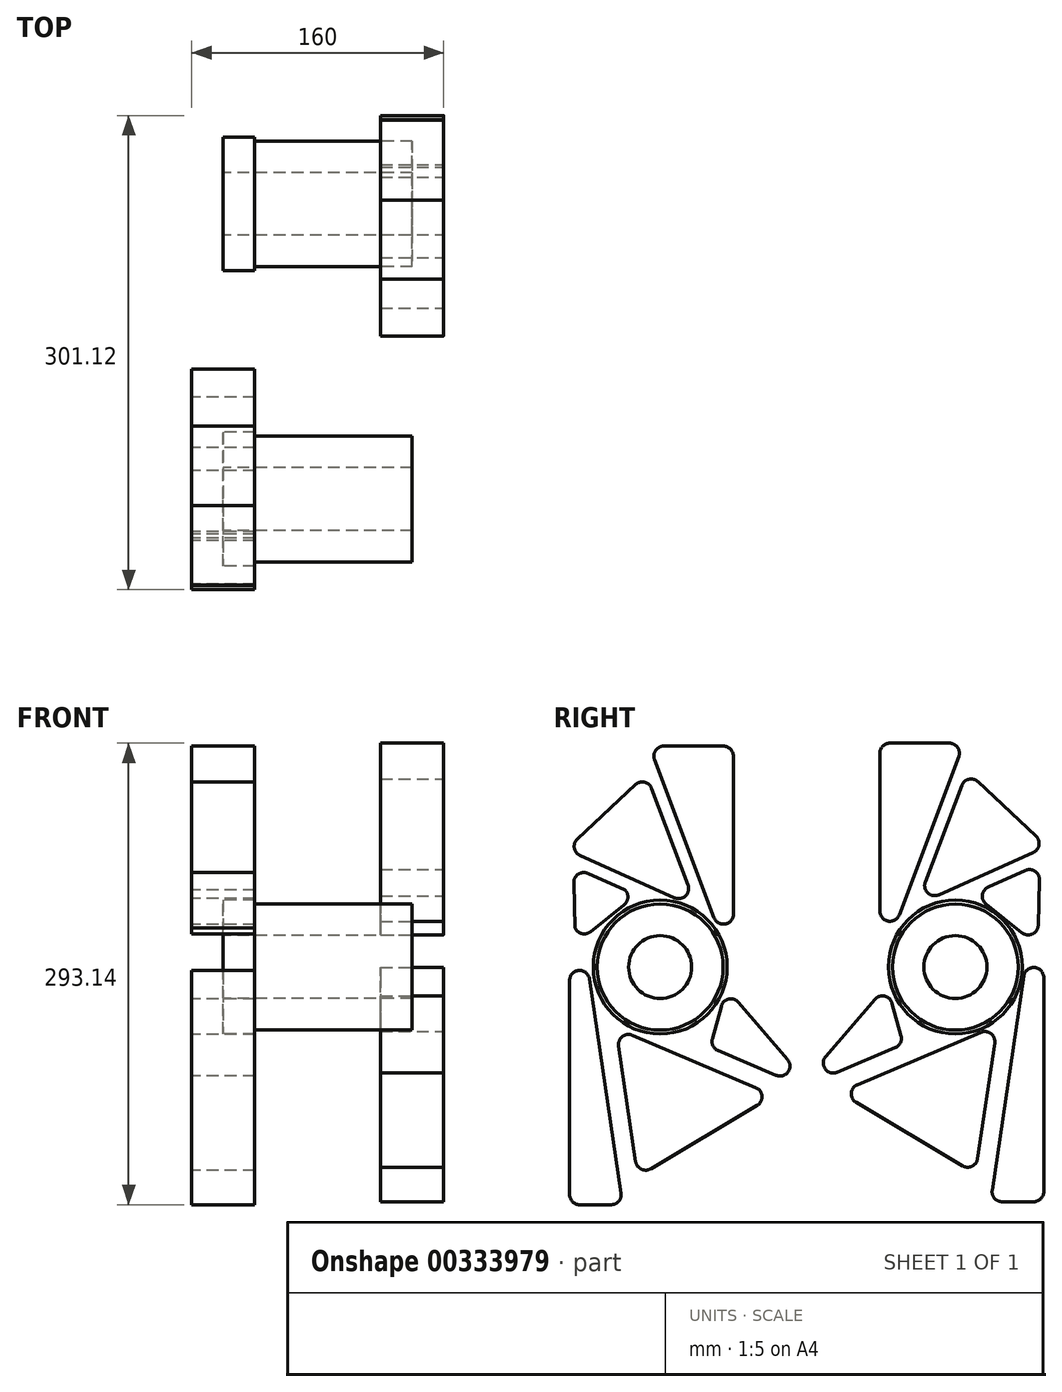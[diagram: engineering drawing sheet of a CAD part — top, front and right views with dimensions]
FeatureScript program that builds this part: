
annotation { "Feature Type Name" : "Feature", "Feature Type Description" : "" }
export const myFeature = defineFeature(function(context is Context, id is Id, definition is map)
    precondition{}
    {
        {
            var Q0;
            Q0=qCreatedBy(makeId("Right.planeOp"),FACE);
            var sketch = newSketch(context, id + "F0", { "sketchPlane" : qUnion([Q0])});
            skLineSegment(sketch, "E0", {"start": v(-158.75, 0) * mm, "end": v(-158.75, 250) * mm});
            skLineSegment(sketch, "E1", {"start": v(-158.75, 250) * mm, "end": v(-93.75, 312.25) * mm});
            skLineSegment(sketch, "E2.MirrorCS", {"start": v(158.75, 250) * mm, "end": v(93.75, 312.25) * mm});
            skLineSegment(sketch, "E3.MirrorCS", {"start": v(158.75, 0) * mm, "end": v(158.75, 250) * mm});
            skLineSegment(sketch, "E4", {"start": v(-158.75, 0) * mm, "end": v(-107.95, 0) * mm});
            skArc(sketch, "E5", {"start": v(107.95, 0) * mm, "mid": v(0, 60.1) * mm, "end": v(-107.95, 0) * mm});
            skLineSegment(sketch, "E6", {"start": v(107.95, 0) * mm, "end": v(158.75, 0) * mm});
            skLineSegment(sketch, "E7", {"start": v(-93.75, 312.25) * mm, "end": v(-40, 312.25) * mm});
            skLineSegment(sketch, "E8", {"start": v(-40, 312.25) * mm, "end": v(-40, 159.85) * mm});
            skArc(sketch, "E9", {"start": v(-40, 159.85) * mm, "mid": v(0, 119.85) * mm, "end": v(40, 159.85) * mm});
            skLineSegment(sketch, "E10", {"start": v(40, 159.85) * mm, "end": v(40, 312.25) * mm});
            skLineSegment(sketch, "E11", {"start": v(40, 312.25) * mm, "end": v(93.75, 312.25) * mm});
            skCircle(sketch, "E12", {"center": v(93.75, 159.85) * mm, "radius": 40 * mm});
            skCircle(sketch, "E13", {"center": v(-93.75, 159.85) * mm, "radius": 40 * mm});
            skSolve(sketch);
        }
        {
            var Q0;
            Q0=makeQuery(id+"F0.imprint","IMPRINT",FACE,{"disambiguationData":[TD([[makeQuery(id+"F0.imprint","IMPRINT",EDGE,{"derivedFrom":sQuery(id+"F0.wireOp",EDGE,"E0")}),-1.0]])]});
            extrude(context, id + "F1", {"entities" : qUnion([Q0]), "endBound" : BoundingType.SYMMETRIC, "depth" : 160 * mm});
        }
        {
            var Q0;
            Q0=makeQuery(id+"F1.opExtrude","SWEPT_FACE",FACE,{"disambiguationData":[OSD([sQuery(id+"F0.wireOp",EDGE,"E3.MirrorCS")])]});
            var sketch = newSketch(context, id + "F2", { "sketchPlane" : qUnion([Q0])});
            skLineSegment(sketch, "E14.bottom", {"start": v(-40, 0) * mm, "end": v(40, 0) * mm});
            skLineSegment(sketch, "E14.top", {"start": v(-40, 330.24) * mm, "end": v(40, 330.24) * mm});
            skLineSegment(sketch, "E14.left", {"start": v(-40, 0) * mm, "end": v(-40, 330.24) * mm});
            skLineSegment(sketch, "E14.right", {"start": v(40, 0) * mm, "end": v(40, 330.24) * mm});
            skSolve(sketch);
        }
        {
            var Q0;
            {var subQ0=sQuery(id+"F2.wireOp",EDGE,"E14.bottom");Q0=makeQuery(id+"F2.imprint","IMPRINT",FACE,{"disambiguationData":[TD([[makeQuery(id+"F2.imprint","IMPRINT",EDGE,{"derivedFrom":subQ0}),1.0]])]});}
            var Q1;
            {var subQ0=sQuery(id+"F2.wireOp",EDGE,"E14.top");Q1=makeQuery(id+"F2.imprint","IMPRINT",FACE,{"disambiguationData":[TD([[makeQuery(id+"F2.imprint","IMPRINT",EDGE,{"derivedFrom":subQ0}),-1.0]])]});}
            extrude(context, id + "F3", {"entities" : qUnion([Q0, Q1]), "operationType" : NewBodyOperationType.REMOVE, "oppositeDirection" : true, "depth" : 414.02 * mm});
        }
        {
            var Q0;
            Q0=makeQuery(id+"F1.opExtrude","CAP_FACE",FACE,{"disambiguationData":[OSD([sQuery(id+"F0.wireOp",EDGE,"E0"),sQuery(id+"F0.wireOp",EDGE,"E1"),sQuery(id+"F0.wireOp",EDGE,"E2.MirrorCS"),sQuery(id+"F0.wireOp",EDGE,"E3.MirrorCS"),sQuery(id+"F0.wireOp",EDGE,"E4"),sQuery(id+"F0.wireOp",EDGE,"E5"),sQuery(id+"F0.wireOp",EDGE,"E6"),sQuery(id+"F0.wireOp",EDGE,"E7"),sQuery(id+"F0.wireOp",EDGE,"E8"),sQuery(id+"F0.wireOp",EDGE,"E9"),sQuery(id+"F0.wireOp",EDGE,"E10"),sQuery(id+"F0.wireOp",EDGE,"E11"),sQuery(id+"F0.wireOp",EDGE,"E12"),sQuery(id+"F0.wireOp",EDGE,"E13")])],"isStart":true});
            var sketch = newSketch(context, id + "F4", { "sketchPlane" : qUnion([Q0])});
            skCircle(sketch, "E15", {"center": v(-93.75, 159.85) * mm, "radius": 42.5 * mm});
            skCircle(sketch, "E16", {"center": v(-93.75, 159.85) * mm, "radius": 20 * mm});
            skCircle(sketch, "E17", {"center": v(93.75, 159.85) * mm, "radius": 42.5 * mm});
            skCircle(sketch, "E18", {"center": v(93.75, 159.85) * mm, "radius": 20 * mm});
            skSolve(sketch);
        }
        {
            var Q0;
            Q0=makeQuery(id+"F4.imprint","IMPRINT",FACE,{"disambiguationData":[TD([[makeQuery(id+"F4.imprint","IMPRINT",EDGE,{"derivedFrom":sQuery(id+"F4.wireOp",EDGE,"E16")}),-1.0]])]});
            var Q1;
            Q1=makeQuery(id+"F4.imprint","IMPRINT",FACE,{"disambiguationData":[TD([[makeQuery(id+"F4.imprint","IMPRINT",EDGE,{"derivedFrom":sQuery(id+"F4.wireOp",EDGE,"E18")}),-1.0]])]});
            extrude(context, id + "F5", {"entities" : qUnion([Q0, Q1]), "operationType" : NewBodyOperationType.ADD, "oppositeDirection" : true, "depth" : 140 * mm});
        }
        {
            var Q0;
            {var subQ0=sQuery(id+"F0.wireOp",EDGE,"E13");var subQ1=sQuery(id+"F0.wireOp",EDGE,"E12");Q0=makeQuery(id+"F5.boolean.opBoolean","MERGE",FACE,{"derivedFrom":[makeQuery(id+"F1.opExtrude","CAP_FACE",FACE,{"disambiguationData":[OSD([sQuery(id+"F0.wireOp",EDGE,"E0"),sQuery(id+"F0.wireOp",EDGE,"E1"),sQuery(id+"F0.wireOp",EDGE,"E2.MirrorCS"),sQuery(id+"F0.wireOp",EDGE,"E3.MirrorCS"),sQuery(id+"F0.wireOp",EDGE,"E4"),sQuery(id+"F0.wireOp",EDGE,"E5"),sQuery(id+"F0.wireOp",EDGE,"E6"),sQuery(id+"F0.wireOp",EDGE,"E7"),sQuery(id+"F0.wireOp",EDGE,"E8"),sQuery(id+"F0.wireOp",EDGE,"E9"),sQuery(id+"F0.wireOp",EDGE,"E10"),sQuery(id+"F0.wireOp",EDGE,"E11"),subQ1,subQ0])],"isStart":true}),makeQuery(id+"F5.opExtrude","CAP_FACE",FACE,{"disambiguationData":[OSD([subQ1,sQuery(id+"F4.wireOp",EDGE,"E16")])],"isStart":true}),makeQuery(id+"F5.opExtrude","CAP_FACE",FACE,{"disambiguationData":[OSD([subQ0,sQuery(id+"F4.wireOp",EDGE,"E18")])],"isStart":true})]});}
            var sketch = newSketch(context, id + "F6", { "sketchPlane" : qUnion([Q0])});
            skCircle(sketch, "E19", {"center": v(-93.75, 159.85) * mm, "radius": 42.5 * mm});
            skCircle(sketch, "E20", {"center": v(93.75, 159.85) * mm, "radius": 42.5 * mm});
            skSolve(sketch);
        }
        {
            var Q0;
            Q0=makeQuery(id+"F6.imprint","IMPRINT",FACE,{"disambiguationData":[TD([[makeQuery(id+"F6.imprint","IMPRINT",EDGE,{"derivedFrom":sQuery(id+"F6.wireOp",EDGE,"E19")}),1.0]])]});
            var Q1;
            Q1=makeQuery(id+"F6.imprint","IMPRINT",FACE,{"disambiguationData":[TD([[makeQuery(id+"F6.imprint","IMPRINT",EDGE,{"derivedFrom":sQuery(id+"F6.wireOp",EDGE,"E20")}),1.0]])]});
            extrude(context, id + "F7", {"entities" : qUnion([Q0, Q1]), "operationType" : NewBodyOperationType.REMOVE, "oppositeDirection" : true, "depth" : 20 * mm});
        }
        {
            var Q0;
            Q0=makeQuery(id+"F1.opExtrude","CAP_FACE",FACE,{"disambiguationData":[OSD([sQuery(id+"F0.wireOp",EDGE,"E0"),sQuery(id+"F0.wireOp",EDGE,"E1"),sQuery(id+"F0.wireOp",EDGE,"E2.MirrorCS"),sQuery(id+"F0.wireOp",EDGE,"E3.MirrorCS"),sQuery(id+"F0.wireOp",EDGE,"E4"),sQuery(id+"F0.wireOp",EDGE,"E5"),sQuery(id+"F0.wireOp",EDGE,"E6"),sQuery(id+"F0.wireOp",EDGE,"E7"),sQuery(id+"F0.wireOp",EDGE,"E8"),sQuery(id+"F0.wireOp",EDGE,"E9"),sQuery(id+"F0.wireOp",EDGE,"E10"),sQuery(id+"F0.wireOp",EDGE,"E11"),sQuery(id+"F0.wireOp",EDGE,"E12"),sQuery(id+"F0.wireOp",EDGE,"E13")])],"isStart":false});
            var sketch = newSketch(context, id + "F8", { "sketchPlane" : qUnion([Q0])});
            skLineSegment(sketch, "E21", {"start": v(-89.93, 302.05) * mm, "end": v(-52.17, 302.05) * mm});
            skLineSegment(sketch, "E22", {"start": v(-45.82, 295.7) * mm, "end": v(-45.82, 195.28) * mm});
            skLineSegment(sketch, "E23", {"start": v(-58.11, 193.04) * mm, "end": v(-95.87, 293.47) * mm});
            skPoint(sketch, "E24.visualSharp", {"position": v(-99.1, 302.05) * mm});
            skArc(sketch, "E24.filletArc", {"start": v(-89.93, 302.05) * mm, "mid": v(-95.15, 299.32) * mm, "end": v(-95.87, 293.47) * mm});
            skPoint(sketch, "E25.visualSharp", {"position": v(-45.82, 302.05) * mm});
            skArc(sketch, "E25.filletArc", {"start": v(-45.82, 295.7) * mm, "mid": v(-47.68, 300.2) * mm, "end": v(-52.17, 302.05) * mm});
            skPoint(sketch, "E26.visualSharp", {"position": v(-45.82, 160.34) * mm});
            skArc(sketch, "E26.filletArc", {"start": v(-58.11, 193.04) * mm, "mid": v(-51.03, 189.03) * mm, "end": v(-45.82, 195.28) * mm});
            skLineSegment(sketch, "E27", {"start": v(-108.02, 277.59) * mm, "end": v(-144.9, 243.03) * mm});
            skLineSegment(sketch, "E28", {"start": v(-143.16, 232.6) * mm, "end": v(-83.18, 205.71) * mm});
            skLineSegment(sketch, "E29", {"start": v(-74.64, 213.74) * mm, "end": v(-97.74, 275.19) * mm});
            skPoint(sketch, "E30.visualSharp", {"position": v(-101.08, 284.09) * mm});
            skArc(sketch, "E30.filletArc", {"start": v(-97.74, 275.19) * mm, "mid": v(-102.24, 279.14) * mm, "end": v(-108.02, 277.59) * mm});
            skPoint(sketch, "E31.visualSharp", {"position": v(-151.87, 236.5) * mm});
            skArc(sketch, "E31.filletArc", {"start": v(-144.9, 243.03) * mm, "mid": v(-146.83, 237.35) * mm, "end": v(-143.16, 232.6) * mm});
            skPoint(sketch, "E32.visualSharp", {"position": v(-69.27, 199.48) * mm});
            skArc(sketch, "E32.filletArc", {"start": v(-83.18, 205.71) * mm, "mid": v(-76.23, 206.88) * mm, "end": v(-74.64, 213.74) * mm});
            skLineSegment(sketch, "E33", {"start": v(-138.24, 221.2) * mm, "end": v(-114.6, 210.6) * mm});
            skLineSegment(sketch, "E34", {"start": v(-113.24, 199.85) * mm, "end": v(-136.05, 181.64) * mm});
            skLineSegment(sketch, "E35", {"start": v(-146.36, 186.43) * mm, "end": v(-147.18, 215.23) * mm});
            skPoint(sketch, "E36.visualSharp", {"position": v(-147.47, 225.34) * mm});
            skArc(sketch, "E36.filletArc", {"start": v(-138.24, 221.2) * mm, "mid": v(-144.36, 220.7) * mm, "end": v(-147.18, 215.23) * mm});
            skPoint(sketch, "E37.visualSharp", {"position": v(-146, 173.7) * mm});
            skArc(sketch, "E37.filletArc", {"start": v(-146.36, 186.43) * mm, "mid": v(-142.68, 180.85) * mm, "end": v(-136.05, 181.64) * mm});
            skPoint(sketch, "E38.visualSharp", {"position": v(-105.1, 206.35) * mm});
            skArc(sketch, "E38.filletArc", {"start": v(-113.24, 199.85) * mm, "mid": v(-110.9, 205.61) * mm, "end": v(-114.6, 210.6) * mm});
            skLineSegment(sketch, "E39", {"start": v(-143.5, 10.77) * mm, "end": v(-123.4, 10.77) * mm});
            skLineSegment(sketch, "E40", {"start": v(-117.1, 18.05) * mm, "end": v(-137.21, 154.14) * mm});
            skLineSegment(sketch, "E41", {"start": v(-149.84, 153.21) * mm, "end": v(-149.84, 17.12) * mm});
            skPoint(sketch, "E42.visualSharp", {"position": v(-149.84, 239.66) * mm});
            skArc(sketch, "E42.filletArc", {"start": v(-137.21, 154.14) * mm, "mid": v(-143.96, 159.54) * mm, "end": v(-149.84, 153.21) * mm});
            skPoint(sketch, "E43.visualSharp", {"position": v(-149.84, 10.77) * mm});
            skArc(sketch, "E43.filletArc", {"start": v(-149.84, 17.12) * mm, "mid": v(-147.98, 12.63) * mm, "end": v(-143.5, 10.77) * mm});
            skPoint(sketch, "E44.visualSharp", {"position": v(-116.03, 10.77) * mm});
            skArc(sketch, "E44.filletArc", {"start": v(-123.4, 10.77) * mm, "mid": v(-118.58, 12.97) * mm, "end": v(-117.1, 18.05) * mm});
            skLineSegment(sketch, "E45", {"start": v(-109.94, 118.4) * mm, "end": v(-31.51, 85.1) * mm});
            skLineSegment(sketch, "E46", {"start": v(-30.74, 73.8) * mm, "end": v(-98.32, 33.57) * mm});
            skLineSegment(sketch, "E47", {"start": v(-107.85, 38.1) * mm, "end": v(-118.7, 111.62) * mm});
            skPoint(sketch, "E48.visualSharp", {"position": v(-120.36, 122.82) * mm});
            skArc(sketch, "E48.filletArc", {"start": v(-109.94, 118.4) * mm, "mid": v(-116.3, 117.57) * mm, "end": v(-118.7, 111.62) * mm});
            skPoint(sketch, "E49.visualSharp", {"position": v(-19.98, 80.2) * mm});
            skArc(sketch, "E49.filletArc", {"start": v(-30.74, 73.8) * mm, "mid": v(-27.66, 79.68) * mm, "end": v(-31.51, 85.1) * mm});
            skPoint(sketch, "E50.visualSharp", {"position": v(-106.46, 28.72) * mm});
            skArc(sketch, "E50.filletArc", {"start": v(-107.85, 38.1) * mm, "mid": v(-104.29, 33.29) * mm, "end": v(-98.32, 33.57) * mm});
            skLineSegment(sketch, "E51", {"start": v(-55.6, 108.64) * mm, "end": v(-18.68, 92.97) * mm});
            skLineSegment(sketch, "E52", {"start": v(-11.38, 102.95) * mm, "end": v(-42.61, 139.31) * mm});
            skLineSegment(sketch, "E53", {"start": v(-53.55, 136.86) * mm, "end": v(-59.24, 116.17) * mm});
            skPoint(sketch, "E54.visualSharp", {"position": v(-50.39, 148.37) * mm});
            skArc(sketch, "E54.filletArc", {"start": v(-42.61, 139.31) * mm, "mid": v(-48.82, 141.37) * mm, "end": v(-53.55, 136.86) * mm});
            skPoint(sketch, "E55.visualSharp", {"position": v(-60.7, 110.81) * mm});
            skArc(sketch, "E55.filletArc", {"start": v(-59.24, 116.17) * mm, "mid": v(-58.83, 111.72) * mm, "end": v(-55.6, 108.64) * mm});
            skPoint(sketch, "E56.visualSharp", {"position": v(6.3, 82.37) * mm});
            skArc(sketch, "E56.filletArc", {"start": v(-18.68, 92.97) * mm, "mid": v(-11.07, 95.07) * mm, "end": v(-11.38, 102.95) * mm});
            skArc(sketch, "E57.MirrorCS", {"start": v(138.24, 221.2) * mm, "mid": v(144.36, 220.7) * mm, "end": v(147.18, 215.23) * mm});
            skArc(sketch, "E58.MirrorCS", {"start": v(45.82, 295.7) * mm, "mid": v(47.68, 300.2) * mm, "end": v(52.17, 302.05) * mm});
            skArc(sketch, "E59.MirrorCS", {"start": v(59.24, 116.17) * mm, "mid": v(58.83, 111.72) * mm, "end": v(55.6, 108.64) * mm});
            skArc(sketch, "E60.MirrorCS", {"start": v(97.74, 275.19) * mm, "mid": v(102.24, 279.14) * mm, "end": v(108.02, 277.59) * mm});
            skArc(sketch, "E61.MirrorCS", {"start": v(144.9, 243.03) * mm, "mid": v(146.83, 237.35) * mm, "end": v(143.16, 232.6) * mm});
            skLineSegment(sketch, "E62.MirrorCS", {"start": v(146.36, 186.43) * mm, "end": v(147.18, 215.23) * mm});
            skArc(sketch, "E63.MirrorCS", {"start": v(89.93, 302.05) * mm, "mid": v(95.15, 299.32) * mm, "end": v(95.87, 293.47) * mm});
            skArc(sketch, "E64.MirrorCS", {"start": v(58.11, 193.04) * mm, "mid": v(51.03, 189.03) * mm, "end": v(45.82, 195.28) * mm});
            skLineSegment(sketch, "E65.MirrorCS", {"start": v(138.24, 221.2) * mm, "end": v(114.6, 210.6) * mm});
            skArc(sketch, "E66.MirrorCS", {"start": v(137.21, 154.14) * mm, "mid": v(143.96, 159.54) * mm, "end": v(149.84, 153.21) * mm});
            skLineSegment(sketch, "E67.MirrorCS", {"start": v(143.5, 10.77) * mm, "end": v(123.4, 10.77) * mm});
            skArc(sketch, "E68.MirrorCS", {"start": v(149.84, 17.12) * mm, "mid": v(147.98, 12.63) * mm, "end": v(143.5, 10.77) * mm});
            skLineSegment(sketch, "E69.MirrorCS", {"start": v(113.24, 199.85) * mm, "end": v(136.05, 181.64) * mm});
            skLineSegment(sketch, "E70.MirrorCS", {"start": v(143.16, 232.6) * mm, "end": v(83.18, 205.71) * mm});
            skArc(sketch, "E71.MirrorCS", {"start": v(83.18, 205.71) * mm, "mid": v(76.23, 206.88) * mm, "end": v(74.64, 213.74) * mm});
            skLineSegment(sketch, "E72.MirrorCS", {"start": v(53.55, 136.86) * mm, "end": v(59.24, 116.17) * mm});
            skArc(sketch, "E73.MirrorCS", {"start": v(146.36, 186.43) * mm, "mid": v(142.68, 180.85) * mm, "end": v(136.05, 181.64) * mm});
            skArc(sketch, "E74.MirrorCS", {"start": v(109.94, 118.4) * mm, "mid": v(116.3, 117.57) * mm, "end": v(118.7, 111.62) * mm});
            skArc(sketch, "E75.MirrorCS", {"start": v(107.85, 38.1) * mm, "mid": v(104.29, 33.29) * mm, "end": v(98.32, 33.57) * mm});
            skArc(sketch, "E76.MirrorCS", {"start": v(123.4, 10.77) * mm, "mid": v(118.58, 12.97) * mm, "end": v(117.1, 18.05) * mm});
            skArc(sketch, "E77.MirrorCS", {"start": v(42.61, 139.31) * mm, "mid": v(48.82, 141.37) * mm, "end": v(53.55, 136.86) * mm});
            skArc(sketch, "E78.MirrorCS", {"start": v(113.24, 199.85) * mm, "mid": v(110.9, 205.61) * mm, "end": v(114.6, 210.6) * mm});
            skArc(sketch, "E79.MirrorCS", {"start": v(30.74, 73.8) * mm, "mid": v(27.66, 79.68) * mm, "end": v(31.51, 85.1) * mm});
            skArc(sketch, "E80.MirrorCS", {"start": v(18.68, 92.97) * mm, "mid": v(11.07, 95.07) * mm, "end": v(11.38, 102.95) * mm});
            skLineSegment(sketch, "E81.MirrorCS", {"start": v(55.6, 108.64) * mm, "end": v(18.68, 92.97) * mm});
            skLineSegment(sketch, "E82.MirrorCS", {"start": v(89.93, 302.05) * mm, "end": v(52.17, 302.05) * mm});
            skPoint(sketch, "E83.MirrorP", {"position": v(69.27, 199.48) * mm});
            skLineSegment(sketch, "E84.MirrorCS", {"start": v(108.02, 277.59) * mm, "end": v(144.9, 243.03) * mm});
            skPoint(sketch, "E85.MirrorP", {"position": v(45.82, 302.05) * mm});
            skPoint(sketch, "E86.MirrorP", {"position": v(147.47, 225.34) * mm});
            skPoint(sketch, "E87.MirrorP", {"position": v(151.87, 236.5) * mm});
            skPoint(sketch, "E88.MirrorP", {"position": v(120.36, 122.82) * mm});
            skPoint(sketch, "E89.MirrorP", {"position": v(101.08, 284.09) * mm});
            skLineSegment(sketch, "E90.MirrorCS", {"start": v(109.94, 118.4) * mm, "end": v(31.51, 85.1) * mm});
            skLineSegment(sketch, "E91.MirrorCS", {"start": v(45.82, 295.7) * mm, "end": v(45.82, 195.28) * mm});
            skLineSegment(sketch, "E92.MirrorCS", {"start": v(58.11, 193.04) * mm, "end": v(95.87, 293.47) * mm});
            skLineSegment(sketch, "E93.MirrorCS", {"start": v(30.74, 73.8) * mm, "end": v(98.32, 33.57) * mm});
            skLineSegment(sketch, "E94.MirrorCS", {"start": v(117.1, 18.05) * mm, "end": v(137.21, 154.14) * mm});
            skPoint(sketch, "E95.MirrorP", {"position": v(19.98, 80.2) * mm});
            skLineSegment(sketch, "E96.MirrorCS", {"start": v(11.38, 102.95) * mm, "end": v(42.61, 139.31) * mm});
            skLineSegment(sketch, "E97.MirrorCS", {"start": v(74.64, 213.74) * mm, "end": v(97.74, 275.19) * mm});
            skPoint(sketch, "E98.MirrorP", {"position": v(-6.3, 82.37) * mm});
            skPoint(sketch, "E99.MirrorP", {"position": v(149.84, 239.66) * mm});
            skLineSegment(sketch, "E100.MirrorCS", {"start": v(107.85, 38.1) * mm, "end": v(118.7, 111.62) * mm});
            skPoint(sketch, "E101.MirrorP", {"position": v(106.46, 28.72) * mm});
            skLineSegment(sketch, "E102.MirrorCS", {"start": v(149.84, 153.21) * mm, "end": v(149.84, 17.12) * mm});
            skPoint(sketch, "E103.MirrorP", {"position": v(116.03, 10.77) * mm});
            skPoint(sketch, "E104.MirrorP", {"position": v(60.7, 110.81) * mm});
            skPoint(sketch, "E105.MirrorP", {"position": v(105.1, 206.35) * mm});
            skPoint(sketch, "E106.MirrorP", {"position": v(99.1, 302.05) * mm});
            skPoint(sketch, "E107.MirrorP", {"position": v(149.84, 10.77) * mm});
            skPoint(sketch, "E108.MirrorP", {"position": v(45.82, 160.34) * mm});
            skPoint(sketch, "E109.MirrorP", {"position": v(146, 173.7) * mm});
            skPoint(sketch, "E110.MirrorP", {"position": v(50.39, 148.37) * mm});
            skLineSegment(sketch, "E111", {"start": v(-6.25, 67.16) * mm, "end": v(6.25, 67.16) * mm});
            skLineSegment(sketch, "E112", {"start": v(11.4, 77.23) * mm, "end": v(5.14, 85.86) * mm});
            skLineSegment(sketch, "E113", {"start": v(-5.14, 85.86) * mm, "end": v(-11.4, 77.23) * mm});
            skPoint(sketch, "E114.visualSharp", {"position": v(0, 92.97) * mm});
            skArc(sketch, "E114.filletArc", {"start": v(5.14, 85.86) * mm, "mid": v(0, 88.49) * mm, "end": v(-5.14, 85.86) * mm});
            skPoint(sketch, "E115.visualSharp", {"position": v(18.68, 67.16) * mm});
            skArc(sketch, "E115.filletArc", {"start": v(6.25, 67.16) * mm, "mid": v(11.9, 70.62) * mm, "end": v(11.4, 77.23) * mm});
            skPoint(sketch, "E116.visualSharp", {"position": v(-18.68, 67.16) * mm});
            skArc(sketch, "E116.filletArc", {"start": v(-11.4, 77.23) * mm, "mid": v(-11.9, 70.62) * mm, "end": v(-6.25, 67.16) * mm});
            skSolve(sketch);
        }
        {
            var Q0;
            Q0=makeQuery(id+"F8.imprint","IMPRINT",FACE,{"disambiguationData":[TD([[makeQuery(id+"F8.imprint","IMPRINT",EDGE,{"derivedFrom":sQuery(id+"F8.wireOp",EDGE,"E27")}),1.0]])]});
            var Q1;
            Q1=makeQuery(id+"F8.imprint","IMPRINT",FACE,{"disambiguationData":[TD([[makeQuery(id+"F8.imprint","IMPRINT",EDGE,{"derivedFrom":sQuery(id+"F8.wireOp",EDGE,"E21")}),-1.0]])]});
            var Q2;
            Q2=makeQuery(id+"F8.imprint","IMPRINT",FACE,{"disambiguationData":[TD([[makeQuery(id+"F8.imprint","IMPRINT",EDGE,{"derivedFrom":sQuery(id+"F8.wireOp",EDGE,"E33")}),-1.0]])]});
            var Q3;
            Q3=makeQuery(id+"F8.imprint","IMPRINT",FACE,{"disambiguationData":[TD([[makeQuery(id+"F8.imprint","IMPRINT",EDGE,{"derivedFrom":sQuery(id+"F8.wireOp",EDGE,"E39")}),1.0]])]});
            var Q4;
            Q4=makeQuery(id+"F8.imprint","IMPRINT",FACE,{"disambiguationData":[TD([[makeQuery(id+"F8.imprint","IMPRINT",EDGE,{"derivedFrom":sQuery(id+"F8.wireOp",EDGE,"E45")}),-1.0]])]});
            var Q5;
            Q5=makeQuery(id+"F8.imprint","IMPRINT",FACE,{"disambiguationData":[TD([[makeQuery(id+"F8.imprint","IMPRINT",EDGE,{"derivedFrom":sQuery(id+"F8.wireOp",EDGE,"E51")}),1.0]])]});
            var Q6;
            Q6=makeQuery(id+"F8.imprint","IMPRINT",FACE,{"disambiguationData":[TD([[makeQuery(id+"F8.imprint","IMPRINT",EDGE,{"derivedFrom":sQuery(id+"F8.wireOp",EDGE,"E111")}),1.0]])]});
            var Q7;
            Q7=makeQuery(id+"F8.imprint","IMPRINT",FACE,{"disambiguationData":[TD([[makeQuery(id+"F8.imprint","IMPRINT",EDGE,{"derivedFrom":sQuery(id+"F8.wireOp",EDGE,"E59.MirrorCS")}),-1.0]])]});
            var Q8;
            Q8=makeQuery(id+"F8.imprint","IMPRINT",FACE,{"disambiguationData":[TD([[makeQuery(id+"F8.imprint","IMPRINT",EDGE,{"derivedFrom":sQuery(id+"F8.wireOp",EDGE,"E74.MirrorCS")}),-1.0]])]});
            var Q9;
            Q9=makeQuery(id+"F8.imprint","IMPRINT",FACE,{"disambiguationData":[TD([[makeQuery(id+"F8.imprint","IMPRINT",EDGE,{"derivedFrom":sQuery(id+"F8.wireOp",EDGE,"E66.MirrorCS")}),-1.0]])]});
            var Q10;
            Q10=makeQuery(id+"F8.imprint","IMPRINT",FACE,{"disambiguationData":[TD([[makeQuery(id+"F8.imprint","IMPRINT",EDGE,{"derivedFrom":sQuery(id+"F8.wireOp",EDGE,"E57.MirrorCS")}),-1.0]])]});
            var Q11;
            Q11=makeQuery(id+"F8.imprint","IMPRINT",FACE,{"disambiguationData":[TD([[makeQuery(id+"F8.imprint","IMPRINT",EDGE,{"derivedFrom":sQuery(id+"F8.wireOp",EDGE,"E60.MirrorCS")}),-1.0]])]});
            var Q12;
            Q12=makeQuery(id+"F8.imprint","IMPRINT",FACE,{"disambiguationData":[TD([[makeQuery(id+"F8.imprint","IMPRINT",EDGE,{"derivedFrom":sQuery(id+"F8.wireOp",EDGE,"E58.MirrorCS")}),-1.0]])]});
            extrude(context, id + "F9", {"entities" : qUnion([Q0, Q1, Q2, Q3, Q4, Q5, Q6, Q7, Q8, Q9, Q10, Q11, Q12]), "operationType" : NewBodyOperationType.REMOVE, "oppositeDirection" : true, "depth" : 49.53 * mm});
        }
        {
            var Q0;
            {var subQ0=sQuery(id+"F0.wireOp",EDGE,"E13");var subQ1=sQuery(id+"F0.wireOp",EDGE,"E12");Q0=makeQuery(id+"F5.boolean.opBoolean","MERGE",FACE,{"derivedFrom":[makeQuery(id+"F1.opExtrude","CAP_FACE",FACE,{"disambiguationData":[OSD([sQuery(id+"F0.wireOp",EDGE,"E0"),sQuery(id+"F0.wireOp",EDGE,"E1"),sQuery(id+"F0.wireOp",EDGE,"E2.MirrorCS"),sQuery(id+"F0.wireOp",EDGE,"E3.MirrorCS"),sQuery(id+"F0.wireOp",EDGE,"E4"),sQuery(id+"F0.wireOp",EDGE,"E5"),sQuery(id+"F0.wireOp",EDGE,"E6"),sQuery(id+"F0.wireOp",EDGE,"E7"),sQuery(id+"F0.wireOp",EDGE,"E8"),sQuery(id+"F0.wireOp",EDGE,"E9"),sQuery(id+"F0.wireOp",EDGE,"E10"),sQuery(id+"F0.wireOp",EDGE,"E11"),subQ1,subQ0])],"isStart":true}),makeQuery(id+"F5.opExtrude","CAP_FACE",FACE,{"disambiguationData":[OSD([subQ1,sQuery(id+"F4.wireOp",EDGE,"E16")])],"isStart":true}),makeQuery(id+"F5.opExtrude","CAP_FACE",FACE,{"disambiguationData":[OSD([subQ0,sQuery(id+"F4.wireOp",EDGE,"E18")])],"isStart":true})]});}
            var sketch = newSketch(context, id + "F10", { "sketchPlane" : qUnion([Q0])});
            skLineSegment(sketch, "E117", {"start": v(-88.49, 300.19) * mm, "end": v(-50.73, 300.19) * mm});
            skLineSegment(sketch, "E118", {"start": v(-44.38, 293.84) * mm, "end": v(-44.38, 193.41) * mm});
            skLineSegment(sketch, "E119", {"start": v(-56.67, 191.18) * mm, "end": v(-94.43, 291.6) * mm});
            skPoint(sketch, "E120.visualSharp", {"position": v(-97.66, 300.19) * mm});
            skArc(sketch, "E120.filletArc", {"start": v(-88.49, 300.19) * mm, "mid": v(-93.7, 297.45) * mm, "end": v(-94.43, 291.6) * mm});
            skPoint(sketch, "E121.visualSharp", {"position": v(-44.38, 300.19) * mm});
            skArc(sketch, "E121.filletArc", {"start": v(-44.38, 293.84) * mm, "mid": v(-46.24, 298.33) * mm, "end": v(-50.73, 300.19) * mm});
            skPoint(sketch, "E122.visualSharp", {"position": v(-44.38, 158.48) * mm});
            skArc(sketch, "E122.filletArc", {"start": v(-56.67, 191.18) * mm, "mid": v(-49.6, 187.16) * mm, "end": v(-44.38, 193.41) * mm});
            skLineSegment(sketch, "E123", {"start": v(-106.58, 275.72) * mm, "end": v(-143.47, 241.17) * mm});
            skLineSegment(sketch, "E124", {"start": v(-141.72, 230.74) * mm, "end": v(-81.74, 203.85) * mm});
            skLineSegment(sketch, "E125", {"start": v(-73.2, 211.88) * mm, "end": v(-96.3, 273.32) * mm});
            skPoint(sketch, "E126.visualSharp", {"position": v(-99.64, 282.22) * mm});
            skArc(sketch, "E126.filletArc", {"start": v(-96.3, 273.32) * mm, "mid": v(-100.8, 277.27) * mm, "end": v(-106.58, 275.72) * mm});
            skPoint(sketch, "E127.visualSharp", {"position": v(-150.43, 234.64) * mm});
            skArc(sketch, "E127.filletArc", {"start": v(-143.47, 241.17) * mm, "mid": v(-145.39, 235.49) * mm, "end": v(-141.72, 230.74) * mm});
            skPoint(sketch, "E128.visualSharp", {"position": v(-67.83, 197.61) * mm});
            skArc(sketch, "E128.filletArc", {"start": v(-81.74, 203.85) * mm, "mid": v(-74.8, 205.01) * mm, "end": v(-73.2, 211.88) * mm});
            skLineSegment(sketch, "E129", {"start": v(-136.8, 219.34) * mm, "end": v(-118.06, 210.94) * mm});
            skLineSegment(sketch, "E130", {"start": v(-116.7, 200.18) * mm, "end": v(-134.78, 185.75) * mm});
            skLineSegment(sketch, "E131", {"start": v(-145.1, 190.53) * mm, "end": v(-145.74, 213.36) * mm});
            skPoint(sketch, "E132.visualSharp", {"position": v(-146.03, 223.48) * mm});
            skArc(sketch, "E132.filletArc", {"start": v(-136.8, 219.34) * mm, "mid": v(-142.92, 218.83) * mm, "end": v(-145.74, 213.36) * mm});
            skPoint(sketch, "E133.visualSharp", {"position": v(-144.73, 177.8) * mm});
            skArc(sketch, "E133.filletArc", {"start": v(-145.1, 190.53) * mm, "mid": v(-141.42, 184.95) * mm, "end": v(-134.78, 185.75) * mm});
            skPoint(sketch, "E134.visualSharp", {"position": v(-108.55, 206.68) * mm});
            skArc(sketch, "E134.filletArc", {"start": v(-116.7, 200.18) * mm, "mid": v(-114.35, 205.94) * mm, "end": v(-118.06, 210.94) * mm});
            skLineSegment(sketch, "E135", {"start": v(-143, 8.9) * mm, "end": v(-121.95, 8.9) * mm});
            skLineSegment(sketch, "E136", {"start": v(-115.68, 16.26) * mm, "end": v(-136.73, 147.74) * mm});
            skLineSegment(sketch, "E137", {"start": v(-149.35, 146.73) * mm, "end": v(-149.35, 15.26) * mm});
            skPoint(sketch, "E138.visualSharp", {"position": v(-149.35, 226.58) * mm});
            skArc(sketch, "E138.filletArc", {"start": v(-136.73, 147.74) * mm, "mid": v(-143.5, 153.06) * mm, "end": v(-149.35, 146.73) * mm});
            skPoint(sketch, "E139.visualSharp", {"position": v(-149.35, 8.9) * mm});
            skArc(sketch, "E139.filletArc", {"start": v(-149.35, 15.26) * mm, "mid": v(-147.49, 10.77) * mm, "end": v(-143, 8.9) * mm});
            skPoint(sketch, "E140.visualSharp", {"position": v(-114.5, 8.9) * mm});
            skArc(sketch, "E140.filletArc", {"start": v(-121.95, 8.9) * mm, "mid": v(-117.12, 11.14) * mm, "end": v(-115.68, 16.26) * mm});
            skLineSegment(sketch, "E141", {"start": v(-109.48, 116.94) * mm, "end": v(-30.07, 83.24) * mm});
            skLineSegment(sketch, "E142", {"start": v(-29.3, 71.93) * mm, "end": v(-96.88, 31.7) * mm});
            skLineSegment(sketch, "E143", {"start": v(-106.4, 36.16) * mm, "end": v(-118.23, 110.1) * mm});
            skPoint(sketch, "E144.visualSharp", {"position": v(-120.04, 121.43) * mm});
            skArc(sketch, "E144.filletArc", {"start": v(-109.48, 116.94) * mm, "mid": v(-115.87, 116.1) * mm, "end": v(-118.23, 110.1) * mm});
            skPoint(sketch, "E145.visualSharp", {"position": v(-18.54, 78.34) * mm});
            skArc(sketch, "E145.filletArc", {"start": v(-29.3, 71.93) * mm, "mid": v(-26.22, 77.82) * mm, "end": v(-30.07, 83.24) * mm});
            skPoint(sketch, "E146.visualSharp", {"position": v(-104.92, 26.92) * mm});
            skArc(sketch, "E146.filletArc", {"start": v(-106.4, 36.16) * mm, "mid": v(-102.81, 31.4) * mm, "end": v(-96.88, 31.7) * mm});
            skLineSegment(sketch, "E147", {"start": v(-54.15, 106.78) * mm, "end": v(-17.24, 91.1) * mm});
            skLineSegment(sketch, "E148", {"start": v(-9.94, 101.09) * mm, "end": v(-41.17, 137.45) * mm});
            skLineSegment(sketch, "E149", {"start": v(-52.11, 135) * mm, "end": v(-57.8, 114.3) * mm});
            skPoint(sketch, "E150.visualSharp", {"position": v(-48.95, 146.5) * mm});
            skArc(sketch, "E150.filletArc", {"start": v(-41.17, 137.45) * mm, "mid": v(-47.38, 139.5) * mm, "end": v(-52.11, 135) * mm});
            skPoint(sketch, "E151.visualSharp", {"position": v(-59.27, 108.95) * mm});
            skArc(sketch, "E151.filletArc", {"start": v(-57.8, 114.3) * mm, "mid": v(-57.39, 109.86) * mm, "end": v(-54.15, 106.78) * mm});
            skPoint(sketch, "E152.visualSharp", {"position": v(7.74, 80.5) * mm});
            skArc(sketch, "E152.filletArc", {"start": v(-17.24, 91.1) * mm, "mid": v(-9.63, 93.2) * mm, "end": v(-9.94, 101.09) * mm});
            skArc(sketch, "E153.MirrorCS", {"start": v(139.68, 219.34) * mm, "mid": v(145.8, 218.83) * mm, "end": v(148.62, 213.36) * mm});
            skArc(sketch, "E154.MirrorCS", {"start": v(47.26, 293.84) * mm, "mid": v(49.12, 298.33) * mm, "end": v(53.6, 300.19) * mm});
            skArc(sketch, "E155.MirrorCS", {"start": v(60.68, 114.3) * mm, "mid": v(60.27, 109.86) * mm, "end": v(57.03, 106.78) * mm});
            skArc(sketch, "E156.MirrorCS", {"start": v(99.18, 273.32) * mm, "mid": v(103.68, 277.27) * mm, "end": v(109.46, 275.72) * mm});
            skArc(sketch, "E157.MirrorCS", {"start": v(146.35, 241.17) * mm, "mid": v(148.27, 235.49) * mm, "end": v(144.6, 230.74) * mm});
            skLineSegment(sketch, "E158.MirrorCS", {"start": v(147.8, 184.56) * mm, "end": v(148.62, 213.36) * mm});
            skArc(sketch, "E159.MirrorCS", {"start": v(91.37, 300.19) * mm, "mid": v(96.59, 297.45) * mm, "end": v(97.31, 291.6) * mm});
            skArc(sketch, "E160.MirrorCS", {"start": v(59.55, 191.18) * mm, "mid": v(52.47, 187.16) * mm, "end": v(47.26, 193.41) * mm});
            skLineSegment(sketch, "E161.MirrorCS", {"start": v(139.68, 219.34) * mm, "end": v(116.04, 208.74) * mm});
            skArc(sketch, "E162.MirrorCS", {"start": v(138.65, 152.27) * mm, "mid": v(145.4, 157.68) * mm, "end": v(151.28, 151.35) * mm});
            skLineSegment(sketch, "E163.MirrorCS", {"start": v(144.93, 8.9) * mm, "end": v(124.83, 8.9) * mm});
            skArc(sketch, "E164.MirrorCS", {"start": v(151.28, 15.26) * mm, "mid": v(149.42, 10.77) * mm, "end": v(144.93, 8.9) * mm});
            skLineSegment(sketch, "E165.MirrorCS", {"start": v(116.65, 199.37) * mm, "end": v(138.08, 182.27) * mm});
            skLineSegment(sketch, "E166.MirrorCS", {"start": v(144.6, 230.74) * mm, "end": v(84.62, 203.85) * mm});
            skArc(sketch, "E167.MirrorCS", {"start": v(84.62, 203.85) * mm, "mid": v(77.67, 205.01) * mm, "end": v(76.08, 211.88) * mm});
            skLineSegment(sketch, "E168.MirrorCS", {"start": v(55, 135) * mm, "end": v(60.68, 114.3) * mm});
            skArc(sketch, "E169.MirrorCS", {"start": v(147.8, 184.56) * mm, "mid": v(143.5, 181.05) * mm, "end": v(138.08, 182.27) * mm});
            skArc(sketch, "E170.MirrorCS", {"start": v(111.38, 116.53) * mm, "mid": v(117.75, 115.7) * mm, "end": v(120.15, 109.76) * mm});
            skArc(sketch, "E171.MirrorCS", {"start": v(109.29, 36.23) * mm, "mid": v(105.73, 31.43) * mm, "end": v(99.76, 31.7) * mm});
            skArc(sketch, "E172.MirrorCS", {"start": v(124.83, 8.9) * mm, "mid": v(120.02, 11.1) * mm, "end": v(118.55, 16.18) * mm});
            skArc(sketch, "E173.MirrorCS", {"start": v(44.05, 137.45) * mm, "mid": v(50.26, 139.5) * mm, "end": v(55, 135) * mm});
            skArc(sketch, "E174.MirrorCS", {"start": v(116.65, 199.37) * mm, "mid": v(114.27, 203.92) * mm, "end": v(116.04, 208.74) * mm});
            skArc(sketch, "E175.MirrorCS", {"start": v(32.18, 71.93) * mm, "mid": v(29.1, 77.82) * mm, "end": v(32.95, 83.24) * mm});
            skArc(sketch, "E176.MirrorCS", {"start": v(20.12, 91.1) * mm, "mid": v(12.51, 93.2) * mm, "end": v(12.82, 101.09) * mm});
            skLineSegment(sketch, "E177.MirrorCS", {"start": v(57.03, 106.78) * mm, "end": v(20.12, 91.1) * mm});
            skLineSegment(sketch, "E178.MirrorCS", {"start": v(91.37, 300.19) * mm, "end": v(53.6, 300.19) * mm});
            skPoint(sketch, "E179.MirrorP", {"position": v(70.71, 197.61) * mm});
            skLineSegment(sketch, "E180.MirrorCS", {"start": v(109.46, 275.72) * mm, "end": v(146.35, 241.17) * mm});
            skPoint(sketch, "E181.MirrorP", {"position": v(47.26, 300.19) * mm});
            skPoint(sketch, "E182.MirrorP", {"position": v(148.91, 223.48) * mm});
            skPoint(sketch, "E183.MirrorP", {"position": v(153.31, 234.64) * mm});
            skPoint(sketch, "E184.MirrorP", {"position": v(121.8, 120.95) * mm});
            skPoint(sketch, "E185.MirrorP", {"position": v(102.52, 282.22) * mm});
            skLineSegment(sketch, "E186.MirrorCS", {"start": v(111.38, 116.53) * mm, "end": v(32.95, 83.24) * mm});
            skLineSegment(sketch, "E187.MirrorCS", {"start": v(47.26, 293.84) * mm, "end": v(47.26, 193.41) * mm});
            skLineSegment(sketch, "E188.MirrorCS", {"start": v(59.55, 191.18) * mm, "end": v(97.31, 291.6) * mm});
            skLineSegment(sketch, "E189.MirrorCS", {"start": v(32.18, 71.93) * mm, "end": v(99.76, 31.7) * mm});
            skLineSegment(sketch, "E190.MirrorCS", {"start": v(118.55, 16.18) * mm, "end": v(138.65, 152.27) * mm});
            skPoint(sketch, "E191.MirrorP", {"position": v(21.42, 78.34) * mm});
            skLineSegment(sketch, "E192.MirrorCS", {"start": v(12.82, 101.09) * mm, "end": v(44.05, 137.45) * mm});
            skLineSegment(sketch, "E193.MirrorCS", {"start": v(76.08, 211.88) * mm, "end": v(99.18, 273.32) * mm});
            skPoint(sketch, "E194.MirrorP", {"position": v(-4.86, 80.5) * mm});
            skPoint(sketch, "E195.MirrorP", {"position": v(151.28, 237.8) * mm});
            skLineSegment(sketch, "E196.MirrorCS", {"start": v(109.29, 36.23) * mm, "end": v(120.15, 109.76) * mm});
            skPoint(sketch, "E197.MirrorP", {"position": v(107.9, 26.86) * mm});
            skLineSegment(sketch, "E198.MirrorCS", {"start": v(151.28, 151.35) * mm, "end": v(151.28, 15.26) * mm});
            skPoint(sketch, "E199.MirrorP", {"position": v(117.48, 8.9) * mm});
            skPoint(sketch, "E200.MirrorP", {"position": v(62.15, 108.95) * mm});
            skPoint(sketch, "E201.MirrorP", {"position": v(106.54, 204.48) * mm});
            skPoint(sketch, "E202.MirrorP", {"position": v(100.54, 300.19) * mm});
            skPoint(sketch, "E203.MirrorP", {"position": v(151.28, 8.9) * mm});
            skPoint(sketch, "E204.MirrorP", {"position": v(47.26, 158.48) * mm});
            skPoint(sketch, "E205.MirrorP", {"position": v(147.44, 171.84) * mm});
            skPoint(sketch, "E206.MirrorP", {"position": v(51.83, 146.5) * mm});
            skLineSegment(sketch, "E207", {"start": v(-4.8, 65.3) * mm, "end": v(7.69, 65.3) * mm});
            skLineSegment(sketch, "E208", {"start": v(12.83, 75.36) * mm, "end": v(6.58, 84) * mm});
            skLineSegment(sketch, "E209", {"start": v(-3.7, 84) * mm, "end": v(-9.95, 75.36) * mm});
            skPoint(sketch, "E210.visualSharp", {"position": v(1.44, 91.1) * mm});
            skArc(sketch, "E210.filletArc", {"start": v(6.58, 84) * mm, "mid": v(1.44, 86.62) * mm, "end": v(-3.7, 84) * mm});
            skPoint(sketch, "E211.visualSharp", {"position": v(20.12, 65.3) * mm});
            skArc(sketch, "E211.filletArc", {"start": v(7.69, 65.3) * mm, "mid": v(13.34, 68.75) * mm, "end": v(12.83, 75.36) * mm});
            skPoint(sketch, "E212.visualSharp", {"position": v(-17.24, 65.3) * mm});
            skArc(sketch, "E212.filletArc", {"start": v(-9.95, 75.36) * mm, "mid": v(-10.46, 68.75) * mm, "end": v(-4.8, 65.3) * mm});
            skSolve(sketch);
        }
        {
            var Q0;
            Q0=makeQuery(id+"F10.imprint","IMPRINT",FACE,{"disambiguationData":[TD([[makeQuery(id+"F10.imprint","IMPRINT",EDGE,{"derivedFrom":sQuery(id+"F10.wireOp",EDGE,"E117")}),-1.0]])]});
            var Q1;
            Q1=makeQuery(id+"F10.imprint","IMPRINT",FACE,{"disambiguationData":[TD([[makeQuery(id+"F10.imprint","IMPRINT",EDGE,{"derivedFrom":sQuery(id+"F10.wireOp",EDGE,"E123")}),1.0]])]});
            var Q2;
            Q2=makeQuery(id+"F10.imprint","IMPRINT",FACE,{"disambiguationData":[TD([[makeQuery(id+"F10.imprint","IMPRINT",EDGE,{"derivedFrom":sQuery(id+"F10.wireOp",EDGE,"E129")}),-1.0]])]});
            var Q3;
            Q3=makeQuery(id+"F10.imprint","IMPRINT",FACE,{"disambiguationData":[TD([[makeQuery(id+"F10.imprint","IMPRINT",EDGE,{"derivedFrom":sQuery(id+"F10.wireOp",EDGE,"E135")}),1.0]])]});
            var Q4;
            Q4=makeQuery(id+"F10.imprint","IMPRINT",FACE,{"disambiguationData":[TD([[makeQuery(id+"F10.imprint","IMPRINT",EDGE,{"derivedFrom":sQuery(id+"F10.wireOp",EDGE,"E141")}),-1.0]])]});
            var Q5;
            Q5=makeQuery(id+"F10.imprint","IMPRINT",FACE,{"disambiguationData":[TD([[makeQuery(id+"F10.imprint","IMPRINT",EDGE,{"derivedFrom":sQuery(id+"F10.wireOp",EDGE,"E147")}),1.0]])]});
            var Q6;
            Q6=makeQuery(id+"F10.imprint","IMPRINT",FACE,{"disambiguationData":[TD([[makeQuery(id+"F10.imprint","IMPRINT",EDGE,{"derivedFrom":sQuery(id+"F10.wireOp",EDGE,"E207")}),1.0]])]});
            var Q7;
            Q7=makeQuery(id+"F10.imprint","IMPRINT",FACE,{"disambiguationData":[TD([[makeQuery(id+"F10.imprint","IMPRINT",EDGE,{"derivedFrom":sQuery(id+"F10.wireOp",EDGE,"E170.MirrorCS")}),-1.0]])]});
            var Q8;
            Q8=makeQuery(id+"F10.imprint","IMPRINT",FACE,{"disambiguationData":[TD([[makeQuery(id+"F10.imprint","IMPRINT",EDGE,{"derivedFrom":sQuery(id+"F10.wireOp",EDGE,"E155.MirrorCS")}),-1.0]])]});
            var Q9;
            Q9=makeQuery(id+"F10.imprint","IMPRINT",FACE,{"disambiguationData":[TD([[makeQuery(id+"F10.imprint","IMPRINT",EDGE,{"derivedFrom":sQuery(id+"F10.wireOp",EDGE,"E162.MirrorCS")}),-1.0]])]});
            var Q10;
            Q10=makeQuery(id+"F10.imprint","IMPRINT",FACE,{"disambiguationData":[TD([[makeQuery(id+"F10.imprint","IMPRINT",EDGE,{"derivedFrom":sQuery(id+"F10.wireOp",EDGE,"E153.MirrorCS")}),-1.0]])]});
            var Q11;
            Q11=makeQuery(id+"F10.imprint","IMPRINT",FACE,{"disambiguationData":[TD([[makeQuery(id+"F10.imprint","IMPRINT",EDGE,{"derivedFrom":sQuery(id+"F10.wireOp",EDGE,"E156.MirrorCS")}),-1.0]])]});
            var Q12;
            Q12=makeQuery(id+"F10.imprint","IMPRINT",FACE,{"disambiguationData":[TD([[makeQuery(id+"F10.imprint","IMPRINT",EDGE,{"derivedFrom":sQuery(id+"F10.wireOp",EDGE,"E154.MirrorCS")}),-1.0]])]});
            extrude(context, id + "F11", {"entities" : qUnion([Q0, Q1, Q2, Q3, Q4, Q5, Q6, Q7, Q8, Q9, Q10, Q11, Q12]), "operationType" : NewBodyOperationType.REMOVE, "oppositeDirection" : true, "depth" : 60.96 * mm});
        }
    });
